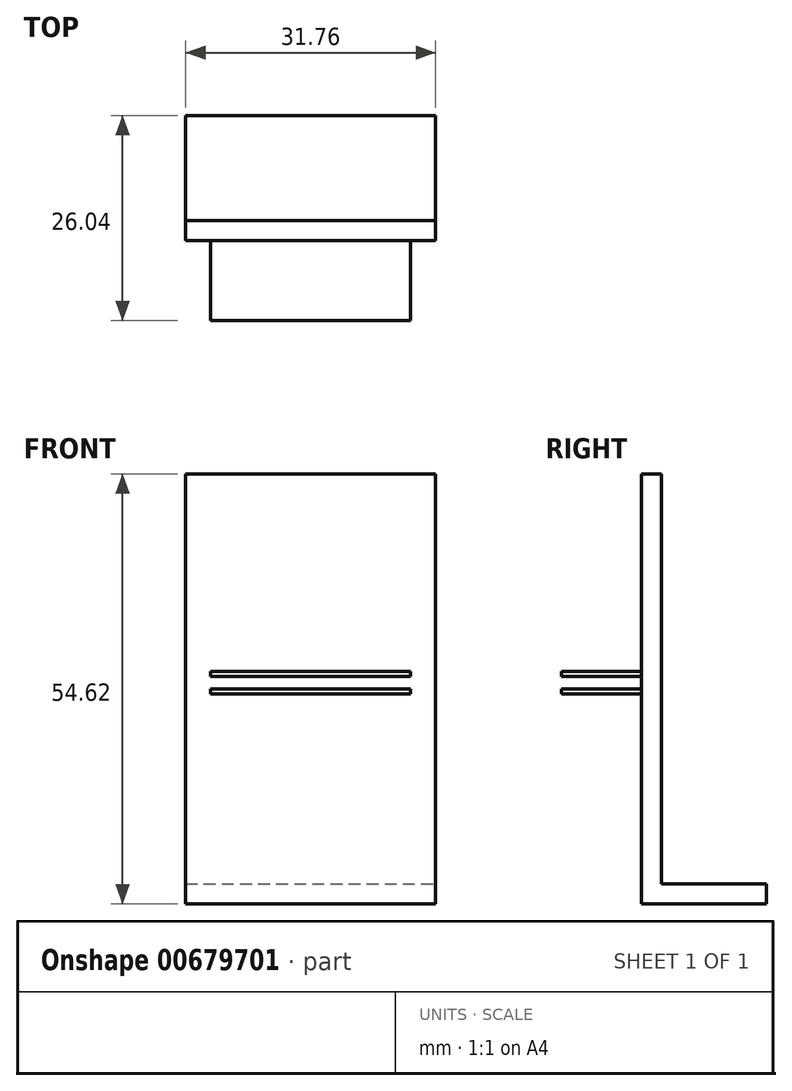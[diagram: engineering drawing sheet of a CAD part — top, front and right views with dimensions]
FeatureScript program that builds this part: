
annotation { "Feature Type Name" : "Feature", "Feature Type Description" : "" }
export const myFeature = defineFeature(function(context is Context, id is Id, definition is map)
    precondition{}
    {
        {
            var Q0;
            Q0=qCreatedBy(makeId("Front.planeOp"),FACE);
            var sketch = newSketch(context, id + "F0", { "sketchPlane" : qUnion([Q0])});
            skLineSegment(sketch, "E0.bottom", {"start": v(15.87, -27.3) * mm, "end": v(-15.88, -27.3) * mm});
            skLineSegment(sketch, "E0.top", {"start": v(15.88, 27.3) * mm, "end": v(-15.87, 27.3) * mm});
            skLineSegment(sketch, "E0.left", {"start": v(15.87, -27.3) * mm, "end": v(15.88, 27.3) * mm});
            skLineSegment(sketch, "E0.right", {"start": v(-15.88, -27.3) * mm, "end": v(-15.87, 27.3) * mm});
            skPoint(sketch, "E0.middle", {"position": v(0, 0) * mm});
            skSolve(sketch);
        }
        {
            var Q0;
            Q0=qCreatedBy(makeId("Front.planeOp"),FACE);
            var sketch = newSketch(context, id + "F1", { "sketchPlane" : qUnion([Q0])});
            skLineSegment(sketch, "E1.bottom", {"start": v(12.7, 2.22) * mm, "end": v(-12.7, 2.22) * mm});
            skLineSegment(sketch, "E1.top", {"start": v(12.7, 1.59) * mm, "end": v(-12.7, 1.59) * mm});
            skLineSegment(sketch, "E1.left", {"start": v(12.7, 2.22) * mm, "end": v(12.7, 1.59) * mm});
            skLineSegment(sketch, "E1.right", {"start": v(-12.7, 2.22) * mm, "end": v(-12.7, 1.59) * mm});
            skLineSegment(sketch, "E2.bottom", {"start": v(12.7, 0) * mm, "end": v(-12.7, 0) * mm});
            skLineSegment(sketch, "E2.top", {"start": v(12.7, -0.64) * mm, "end": v(-12.7, -0.64) * mm});
            skLineSegment(sketch, "E2.left", {"start": v(12.7, 0) * mm, "end": v(12.7, -0.64) * mm});
            skLineSegment(sketch, "E2.right", {"start": v(-12.7, 0) * mm, "end": v(-12.7, -0.64) * mm});
            skSolve(sketch);
        }
        {
            var Q0;
            Q0=makeQuery(id+"F0.imprint","IMPRINT",FACE,{"disambiguationData":[TD([[makeQuery(id+"F0.imprint","IMPRINT",EDGE,{"derivedFrom":sQuery(id+"F0.wireOp",EDGE,"E0.bottom")}),-1.0]])]});
            var sketch = newSketch(context, id + "F2", { "sketchPlane" : qUnion([Q0])});
            skSolve(sketch);
        }
        {
            var Q0;
            Q0 = qSketchRegion(id + "F1", true);
            extrude(context, id + "F3", {"entities" : qUnion([Q0]), "depth" : 10.16 * mm, "offsetDistance" : 25.4 * mm});
        }
        {
            var Q0;
            Q0=makeQuery(id+"F2.imprint","IMPRINT",FACE,{"disambiguationData":[TD([[makeQuery(id+"F2.imprint","IMPRINT",EDGE,{"derivedFrom":makeQuery(id+"F0.imprint","IMPRINT",EDGE,{"derivedFrom":sQuery(id+"F0.wireOp",EDGE,"E0.bottom")})}),-1.0]])]});
            extrude(context, id + "F4", {"entities" : qUnion([Q0]), "oppositeDirection" : true, "depth" : 2.54 * mm, "offsetDistance" : 25.4 * mm});
        }
        {
            var Q0;
            Q0=qCreatedBy(makeId("Front.planeOp"),FACE);
            var sketch = newSketch(context, id + "F5", { "sketchPlane" : qUnion([Q0])});
            skLineSegment(sketch, "E3.bottom", {"start": v(-15.87, -27.32) * mm, "end": v(15.87, -27.32) * mm});
            skLineSegment(sketch, "E3.top", {"start": v(-15.87, -24.78) * mm, "end": v(15.87, -24.78) * mm});
            skLineSegment(sketch, "E3.left", {"start": v(-15.87, -27.32) * mm, "end": v(-15.87, -24.78) * mm});
            skLineSegment(sketch, "E3.right", {"start": v(15.87, -27.32) * mm, "end": v(15.87, -24.78) * mm});
            skPoint(sketch, "E3.middle", {"position": v(0, -26.05) * mm});
            skSolve(sketch);
        }
        {
            var Q0;
            Q0 = qSketchRegion(id + "F5", true);
            extrude(context, id + "F6", {"entities" : qUnion([Q0]), "operationType" : NewBodyOperationType.ADD, "oppositeDirection" : true, "depth" : 15.88 * mm, "offsetDistance" : 25.4 * mm});
        }
    });
